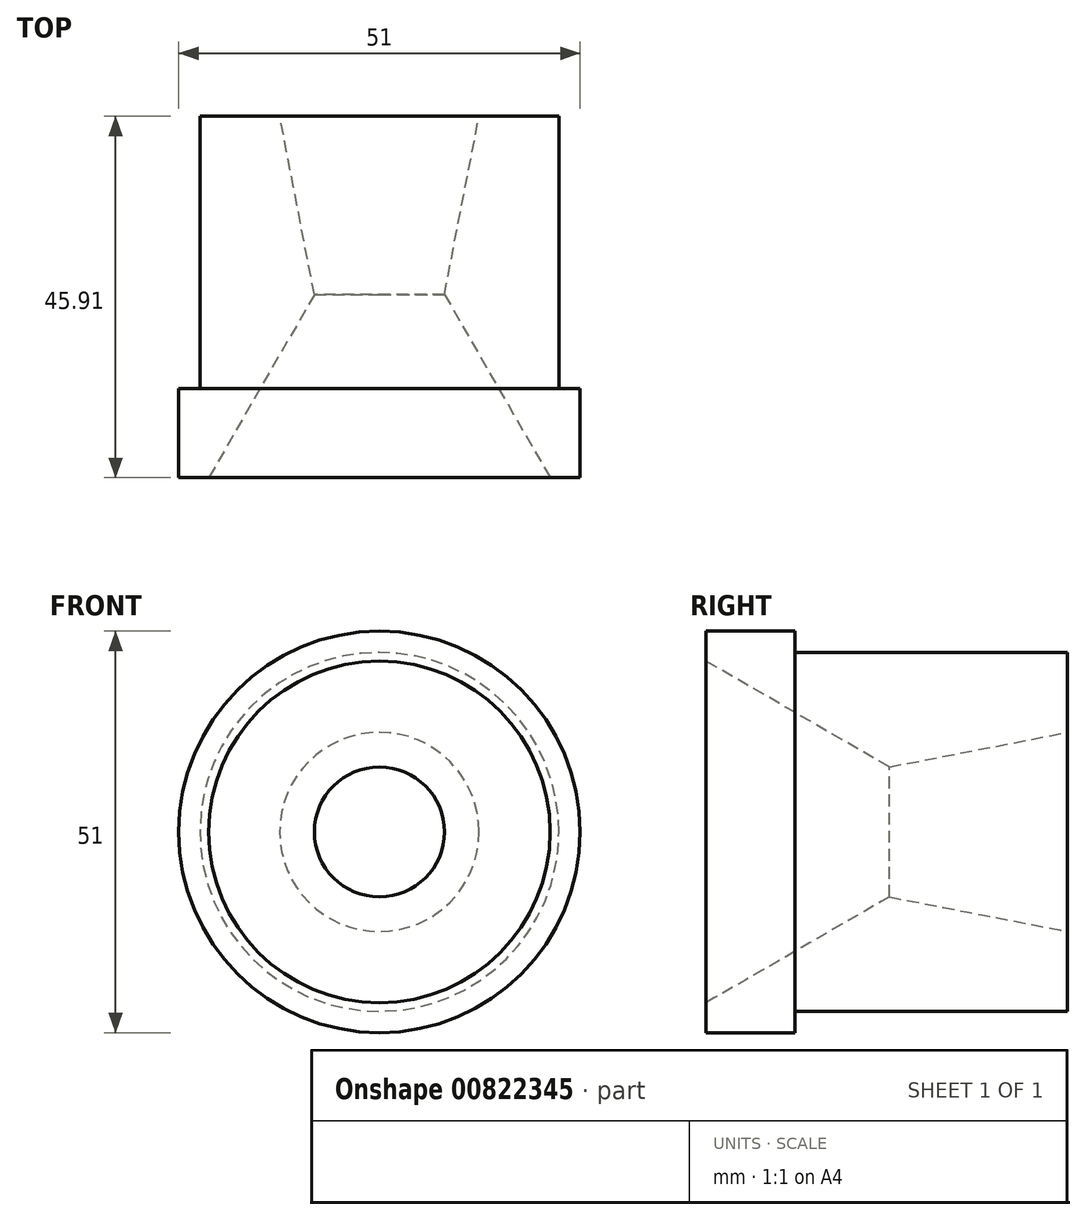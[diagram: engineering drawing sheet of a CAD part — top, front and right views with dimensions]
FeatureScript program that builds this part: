
annotation { "Feature Type Name" : "Feature", "Feature Type Description" : "" }
export const myFeature = defineFeature(function(context is Context, id is Id, definition is map)
    precondition{}
    {
        {
            var Q0;
            Q0=qCreatedBy(makeId("Front.planeOp"),FACE);
            var sketch = newSketch(context, id + "F0", { "sketchPlane" : qUnion([Q0])});
            skCircle(sketch, "E0", {"center": v(0, 0) * mm, "radius": 25.5 * mm});
            skSolve(sketch);
        }
        {
            var Q0;
            Q0=makeQuery(id+"F0.imprint","IMPRINT",FACE,{"disambiguationData":[TD([[makeQuery(id+"F0.imprint","IMPRINT",EDGE,{"derivedFrom":sQuery(id+"F0.wireOp",EDGE,"E0")}),1.0]])]});
            extrude(context, id + "F1", {"entities" : qUnion([Q0]), "oppositeDirection" : true, "depth" : 11.3 * mm, "offsetDistance" : 25 * mm});
        }
        {
            var Q0;
            Q0=makeQuery(id+"F1.opExtrude","CAP_FACE",FACE,{"disambiguationData":[OSD([sQuery(id+"F0.wireOp",EDGE,"E0")])],"isStart":false});
            var sketch = newSketch(context, id + "F2", { "sketchPlane" : qUnion([Q0])});
            skCircle(sketch, "E1", {"center": v(0, 0) * mm, "radius": 22.8 * mm});
            skSolve(sketch);
        }
        {
            var Q0;
            Q0=makeQuery(id+"F1.opExtrude","CAP_FACE",FACE,{"disambiguationData":[OSD([sQuery(id+"F0.wireOp",EDGE,"E0")])],"isStart":false});
            cPlane(context, id + "F3", {"entities" : qUnion([Q0]), "cplaneType" : CPlaneType.OFFSET, "offset" : 0 * mm, "width" : 152.4 * mm, "height" : 152.4 * mm});
        }
        {
            var Q0;
            Q0=qCreatedBy(makeId("Right.planeOp"),FACE);
            var sketch = newSketch(context, id + "F4", { "sketchPlane" : qUnion([Q0])});
            skLineSegment(sketch, "E2", {"start": v(0, 0) * mm, "end": v(0, 21.7) * mm});
            skLineSegment(sketch, "E3", {"start": v(0, 21.7) * mm, "end": v(23.27, 8.26) * mm});
            skLineSegment(sketch, "E4", {"start": v(23.27, 8.26) * mm, "end": v(23.27, 0) * mm});
            skLineSegment(sketch, "E5", {"start": v(0, 0) * mm, "end": v(23.27, 0) * mm});
            skLineSegment(sketch, "E6", {"start": v(23.27, 8.25) * mm, "end": v(45.9, 12.65) * mm});
            skLineSegment(sketch, "E7", {"start": v(45.9, 12.65) * mm, "end": v(45.9, 0) * mm});
            skLineSegment(sketch, "E8", {"start": v(45.9, 0) * mm, "end": v(23.27, 0) * mm});
            skLineSegment(sketch, "E9", {"start": v(23.27, 8.26) * mm, "end": v(45.9, 8.26) * mm});
            skSolve(sketch);
        }
        {
            var Q0;
            Q0=makeQuery(id+"F2.imprint","IMPRINT",FACE,{"disambiguationData":[TD([[makeQuery(id+"F2.imprint","IMPRINT",EDGE,{"derivedFrom":sQuery(id+"F2.wireOp",EDGE,"E1")}),1.0]])]});
            var Q1;
            Q1=sQuery(id+"F4.wireOp",VERTEX,"E7.end");
            extrude(context, id + "F5", {"entities" : qUnion([Q0]), "operationType" : NewBodyOperationType.ADD, "endBound" : BoundingType.UP_TO_VERTEX, "depth" : 25.4 * mm, "endBoundEntityVertex" : qUnion([Q1]), "offsetDistance" : 25.4 * mm});
        }
        {
            var Q0;
            Q0 = qSketchRegion(id + "F4", true);
            var Q1;
            Q1=sQuery(id+"F4.wireOp",EDGE,"E5");
            revolve(context, id + "F6", {"operationType" : NewBodyOperationType.REMOVE, "surfaceOperationType" : NewSurfaceOperationType.NEW, "entities" : qUnion([Q0]), "axis" : qUnion([Q1]), "revolveType" : RevolveType.FULL});
        }
    });
